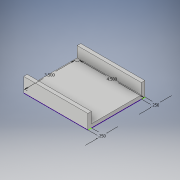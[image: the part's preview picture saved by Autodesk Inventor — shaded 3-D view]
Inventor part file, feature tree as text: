
AUTODESK INVENTOR PART (.ipt)
format: ipt  version: 2019 (Build 230136000, 136)  size: 106,496 bytes
history: native  units: in
note: dims shown in document units (in); Inventor stores cm internally (conversion verified against a paired STEP export)
features: extrude x2, sketch x1
ambient origin geometry x8: Origin, YZ Plane, XZ Plane, XY Plane, X Axis, Y Axis, Z Axis, Center Point
bodies: Solid1 (feature_tree)
feature tree (3):
  sketch  "Sketch1"  dims[d0=4.5in d1=3.5in d2=0.25in d3=0.25in d4=0.25in d5=0.0in d6=1.0in d7=0.0in]
  extrude  "Extrusion1"  Depth=3.5in
  extrude  "Extrusion2"  Depth=0.25in
